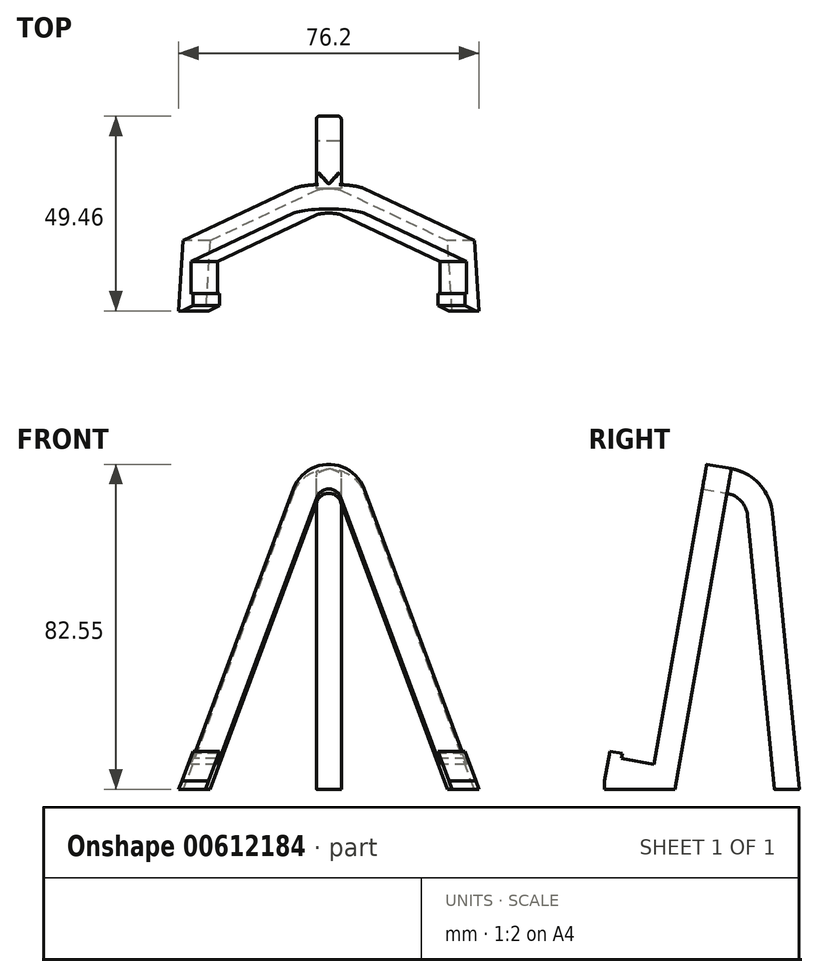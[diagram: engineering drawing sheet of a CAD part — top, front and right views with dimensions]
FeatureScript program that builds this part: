
annotation { "Feature Type Name" : "Feature", "Feature Type Description" : "" }
export const myFeature = defineFeature(function(context is Context, id is Id, definition is map)
    precondition{}
    {
        {
            var Q0;
            Q0=qCreatedBy(makeId("Right.planeOp"),FACE);
            var sketch = newSketch(context, id + "F0", { "sketchPlane" : qUnion([Q0])});
            skLineSegment(sketch, "E0", {"start": v(0, 0) * mm, "end": v(6.45, 0) * mm});
            skLineSegment(sketch, "E1", {"start": v(14.56, 82.55) * mm, "end": v(1.12, 6.35) * mm});
            skLineSegment(sketch, "E2", {"start": v(1.12, 6.35) * mm, "end": v(-7.13, 7.8) * mm});
            skLineSegment(sketch, "E3", {"start": v(-7.13, 7.8) * mm, "end": v(-6.91, 9.06) * mm});
            skLineSegment(sketch, "E4", {"start": v(-6.91, 9.06) * mm, "end": v(-10.04, 9.6) * mm});
            skLineSegment(sketch, "E5", {"start": v(-10.04, 9.6) * mm, "end": v(-11.36, 2.1) * mm});
            skLineSegment(sketch, "E6", {"start": v(14.56, 82.55) * mm, "end": v(20.8, 81.45) * mm});
            skLineSegment(sketch, "E7", {"start": v(20.8, 81.45) * mm, "end": v(12.8, 36.01) * mm});
            skLineSegment(sketch, "E8.trimOffspring", {"start": v(12.8, 36.01) * mm, "end": v(6.45, 0) * mm});
            skLineSegment(sketch, "E9", {"start": v(-11.36, 2.1) * mm, "end": v(-11.36, 0) * mm});
            skLineSegment(sketch, "E10", {"start": v(-11.36, 0) * mm, "end": v(0, 0) * mm});
            skSolve(sketch);
        }
        {
            var Q0;
            Q0=makeQuery(id+"F0.imprint","IMPRINT",FACE,{"disambiguationData":[TD([[makeQuery(id+"F0.imprint","IMPRINT",EDGE,{"derivedFrom":sQuery(id+"F0.wireOp",EDGE,"E0")}),1.0]])]});
            extrude(context, id + "F1", {"entities" : qUnion([Q0]), "endBound" : BoundingType.SYMMETRIC, "depth" : 76.2 * mm, "offsetDistance" : 25.4 * mm});
        }
        {
            var Q0;
            Q0=makeQuery(id+"F1.opExtrude","SWEPT_FACE",FACE,{"disambiguationData":[OSD([sQuery(id+"F0.wireOp",EDGE,"E1")])]});
            var sketch = newSketch(context, id + "F2", { "sketchPlane" : qUnion([Q0])});
            skLineSegment(sketch, "E11", {"start": v(-31.34, -1.97) * mm, "end": v(-2.98, 75.4) * mm});
            skLineSegment(sketch, "E12", {"start": v(2.98, 75.4) * mm, "end": v(31.34, -1.97) * mm});
            skLineSegment(sketch, "E13", {"start": v(38.1, -1.97) * mm, "end": v(31.34, -1.97) * mm});
            skLineSegment(sketch, "E14", {"start": v(38.1, -1.97) * mm, "end": v(8.94, 77.58) * mm});
            skLineSegment(sketch, "E15", {"start": v(-8.94, 77.58) * mm, "end": v(-38.1, -1.97) * mm});
            skLineSegment(sketch, "E16", {"start": v(-31.34, -1.97) * mm, "end": v(-38.1, -1.97) * mm});
            skPoint(sketch, "E17.visualSharp", {"position": v(0, 101.98) * mm});
            skArc(sketch, "E17.filletArc", {"start": v(8.94, 77.58) * mm, "mid": v(0, 83.82) * mm, "end": v(-8.94, 77.58) * mm});
            skPoint(sketch, "E18.visualSharp", {"position": v(0, 83.52) * mm});
            skArc(sketch, "E18.filletArc", {"start": v(2.98, 75.4) * mm, "mid": v(0, 77.47) * mm, "end": v(-2.98, 75.4) * mm});
            skSolve(sketch);
        }
        {
            var Q0;
            Q0 = qSketchRegion(id + "F2", true);
            extrude(context, id + "F3", {"entities" : qUnion([Q0]), "operationType" : NewBodyOperationType.INTERSECT, "endBound" : BoundingType.THROUGH_ALL, "depth" : 25.4 * mm, "offsetDistance" : 25.4 * mm, "hasSecondDirection" : true, "secondDirectionBound" : SecondDirectionBoundingType.THROUGH_ALL, "secondDirectionOppositeDirection" : true, "secondDirectionDepth" : 25.4 * mm});
        }
        {
            var Q0;
            Q0=qCreatedBy(makeId("Right.planeOp"),FACE);
            var sketch = newSketch(context, id + "F4", { "sketchPlane" : qUnion([Q0])});
            skLineSegment(sketch, "E19", {"start": v(38.1, 0) * mm, "end": v(31.72, 0) * mm});
            skLineSegment(sketch, "E20", {"start": v(19.7, 75.2) * mm, "end": v(20.8, 81.45) * mm});
            skLineSegment(sketch, "E21", {"start": v(38.1, 0) * mm, "end": v(31.24, 70.18) * mm});
            skLineSegment(sketch, "E22", {"start": v(31.72, 0) * mm, "end": v(24.92, 69.56) * mm});
            skArc(sketch, "E23", {"start": v(31.24, 70.18) * mm, "mid": v(27.92, 77.57) * mm, "end": v(20.8, 81.45) * mm});
            skArc(sketch, "E24", {"start": v(24.92, 69.56) * mm, "mid": v(23.26, 73.25) * mm, "end": v(19.7, 75.2) * mm});
            skLineSegment(sketch, "E25", {"start": v(20.8, 81.45) * mm, "end": v(14.63, 82.54) * mm, "construction": true});
            skLineSegment(sketch, "E26", {"start": v(19.7, 75.2) * mm, "end": v(13.51, 76.29) * mm, "construction": true});
            skSolve(sketch);
        }
        {
            var Q0;
            Q0=makeQuery(id+"F4.imprint","IMPRINT",FACE,{"disambiguationData":[TD([[makeQuery(id+"F4.imprint","IMPRINT",EDGE,{"derivedFrom":sQuery(id+"F4.wireOp",EDGE,"E19")}),-1.0]])]});
            extrude(context, id + "F5", {"entities" : qUnion([Q0]), "operationType" : NewBodyOperationType.ADD, "endBound" : BoundingType.SYMMETRIC, "depth" : 6.35 * mm, "offsetDistance" : 25.4 * mm});
        }
        {
            var Q0;
            Q0=makeQuery(id+"F1.opExtrude","SWEPT_FACE",FACE,{"disambiguationData":[OSD([sQuery(id+"F0.wireOp",EDGE,"E1")])]});
            var sketch = newSketch(context, id + "F6", { "sketchPlane" : qUnion([Q0])});
            skArc(sketch, "E27.0", {"start": v(8.94, 77.58) * mm, "mid": v(0, 83.82) * mm, "end": v(-8.94, 77.58) * mm});
            skLineSegment(sketch, "E28", {"start": v(-8.94, 77.58) * mm, "end": v(-8.94, 85.44) * mm});
            skLineSegment(sketch, "E29", {"start": v(-8.94, 85.44) * mm, "end": v(8.94, 85.76) * mm});
            skLineSegment(sketch, "E30", {"start": v(8.94, 85.76) * mm, "end": v(8.94, 77.58) * mm});
            skSolve(sketch);
        }
        {
            var Q0;
            Q0 = qSketchRegion(id + "F6", true);
            extrude(context, id + "F7", {"entities" : qUnion([Q0]), "operationType" : NewBodyOperationType.REMOVE, "endBound" : BoundingType.THROUGH_ALL, "oppositeDirection" : true, "depth" : 25.4 * mm, "offsetDistance" : 25.4 * mm});
        }
        {
            var Q0;
            Q0=makeQuery(id+"F3.boolean.opBoolean","INTERSECT",EDGE,{"derivedFrom":[makeQuery(id+"F1.opExtrude","SWEPT_FACE",FACE,{"disambiguationData":[OSD([sQuery(id+"F0.wireOp",EDGE,"E1")])]}),makeQuery(id+"F3.boolean.toolComplement.opBoolean","COPY",FACE,{"derivedFrom":makeQuery(id+"F3.opExtrude","SWEPT_FACE",FACE,{"disambiguationData":[OSD([sQuery(id+"F2.wireOp",EDGE,"E14")])]})})]});
            var Q1;
            Q1=makeQuery(id+"F7.boolean.opBoolean","INTERSECT",EDGE,{"derivedFrom":[makeQuery(id+"F5.opExtrude","CAP_FACE",FACE,{"disambiguationData":[OSD([sQuery(id+"F4.wireOp",EDGE,"E19"),sQuery(id+"F4.wireOp",EDGE,"E20"),sQuery(id+"F4.wireOp",EDGE,"E21"),sQuery(id+"F4.wireOp",EDGE,"E22"),sQuery(id+"F4.wireOp",EDGE,"E23"),sQuery(id+"F4.wireOp",EDGE,"E24")])],"isStart":false}),makeQuery(id+"F7.opExtrude","SWEPT_FACE",FACE,{"disambiguationData":[OSD([sQuery(id+"F6.wireOp",EDGE,"E27.0")])]})]});
            var Q2;
            Q2=makeQuery(id+"F5.opExtrude","CAP_EDGE",EDGE,{"disambiguationData":[OSD([sQuery(id+"F4.wireOp",EDGE,"E23")])],"isStart":false});
            var Q3;
            {var subQ0=makeQuery(id+"F3.boolean.toolComplement.opBoolean","COPY",FACE,{"derivedFrom":makeQuery(id+"F3.opExtrude","SWEPT_FACE",FACE,{"disambiguationData":[OSD([sQuery(id+"F2.wireOp",EDGE,"E17.filletArc")])]})});var subQ1=makeQuery(id+"F3.boolean.opBoolean","COPY",FACE,{"derivedFrom":subQ0});var subQ3=makeQuery(id+"F1.opExtrude","SWEPT_FACE",FACE,{"disambiguationData":[OSD([sQuery(id+"F0.wireOp",EDGE,"E7"),sQuery(id+"F0.wireOp",EDGE,"E8.trimOffspring")])]});Q3=makeQuery(id+"F5.boolean.opBoolean","SPLIT",EDGE,{"disambiguationData":[topologyDisambiguationEdgeConnected([subQ3,subQ1]),TD([makeQuery(id+"F3.boolean.opBoolean","COPY",FACE,{"derivedFrom":makeQuery(id+"F3.boolean.toolComplement.opBoolean","COPY",FACE,{"derivedFrom":makeQuery(id+"F3.opExtrude","SWEPT_FACE",FACE,{"disambiguationData":[OSD([sQuery(id+"F2.wireOp",EDGE,"E14")])]})})})])],"derivedFrom":makeQuery(id+"F3.boolean.opBoolean","INTERSECT",EDGE,{"derivedFrom":[subQ3,subQ0]})});}
            var Q4;
            Q4=makeQuery(id+"F3.boolean.opBoolean","INTERSECT",EDGE,{"derivedFrom":[makeQuery(id+"F1.opExtrude","SWEPT_FACE",FACE,{"disambiguationData":[OSD([sQuery(id+"F0.wireOp",EDGE,"E2")])]}),makeQuery(id+"F3.boolean.toolComplement.opBoolean","COPY",FACE,{"derivedFrom":makeQuery(id+"F3.opExtrude","SWEPT_FACE",FACE,{"disambiguationData":[OSD([sQuery(id+"F2.wireOp",EDGE,"E14")])]})})]});
            var Q5;
            Q5=makeQuery(id+"F3.boolean.opBoolean","INTERSECT",EDGE,{"derivedFrom":[makeQuery(id+"F1.opExtrude","SWEPT_FACE",FACE,{"disambiguationData":[OSD([sQuery(id+"F0.wireOp",EDGE,"E3")])]}),makeQuery(id+"F3.boolean.toolComplement.opBoolean","COPY",FACE,{"derivedFrom":makeQuery(id+"F3.opExtrude","SWEPT_FACE",FACE,{"disambiguationData":[OSD([sQuery(id+"F2.wireOp",EDGE,"E14")])]})})]});
            var Q6;
            Q6=makeQuery(id+"F3.boolean.opBoolean","INTERSECT",EDGE,{"derivedFrom":[makeQuery(id+"F1.opExtrude","SWEPT_FACE",FACE,{"disambiguationData":[OSD([sQuery(id+"F0.wireOp",EDGE,"E4")])]}),makeQuery(id+"F3.boolean.toolComplement.opBoolean","COPY",FACE,{"derivedFrom":makeQuery(id+"F3.opExtrude","SWEPT_FACE",FACE,{"disambiguationData":[OSD([sQuery(id+"F2.wireOp",EDGE,"E14")])]})})]});
            var Q7;
            Q7=makeQuery(id+"F3.boolean.opBoolean","INTERSECT",EDGE,{"derivedFrom":[makeQuery(id+"F1.opExtrude","SWEPT_FACE",FACE,{"disambiguationData":[OSD([sQuery(id+"F0.wireOp",EDGE,"E5")])]}),makeQuery(id+"F3.boolean.toolComplement.opBoolean","COPY",FACE,{"derivedFrom":makeQuery(id+"F3.opExtrude","SWEPT_FACE",FACE,{"disambiguationData":[OSD([sQuery(id+"F2.wireOp",EDGE,"E14")])]})})]});
            var Q8;
            Q8=makeQuery(id+"F3.boolean.opBoolean","MERGE",EDGE,{"derivedFrom":[makeQuery(id+"F1.opExtrude","CAP_EDGE",EDGE,{"disambiguationData":[OSD([sQuery(id+"F0.wireOp",EDGE,"PjRodM2x-iDPi-nF9E-hlY8-18HYTHsXEe14")])],"isStart":false}),makeQuery(id+"F3.boolean.toolComplement.opBoolean","COPY",EDGE,{"derivedFrom":makeQuery(id+"F3.opExtrude","SWEPT_EDGE",EDGE,{"disambiguationData":[OSD([sQuery(id+"F2.wireOp",EDGE,"E13"),sQuery(id+"F2.wireOp",EDGE,"E14")])]})})]});
            var Q9;
            {var subQ0=sQuery(id+"F0.wireOp",EDGE,"E5");var subQ1=sQuery(id+"F0.wireOp",EDGE,"PjRodM2x-iDPi-nF9E-hlY8-18HYTHsXEe14");Q9=makeQuery(id+"F3.boolean.opBoolean","SPLIT",EDGE,{"disambiguationData":[TD([makeQuery(id+"F3.boolean.toolComplement.opBoolean","COPY",FACE,{"derivedFrom":makeQuery(id+"F3.opExtrude","SWEPT_FACE",FACE,{"disambiguationData":[OSD([sQuery(id+"F2.wireOp",EDGE,"E12")])]})})])],"derivedFrom":makeQuery(id+"F1.opExtrude","SWEPT_EDGE",EDGE,{"disambiguationData":[OSD([subQ0,subQ1])]})});}
            var Q10;
            Q10=makeQuery(id+"F3.boolean.opBoolean","INTERSECT",EDGE,{"derivedFrom":[makeQuery(id+"F1.opExtrude","SWEPT_FACE",FACE,{"disambiguationData":[OSD([sQuery(id+"F0.wireOp",EDGE,"E5")])]}),makeQuery(id+"F3.boolean.toolComplement.opBoolean","COPY",FACE,{"derivedFrom":makeQuery(id+"F3.opExtrude","SWEPT_FACE",FACE,{"disambiguationData":[OSD([sQuery(id+"F2.wireOp",EDGE,"E12")])]})})]});
            var Q11;
            {var subQ0=sQuery(id+"F0.wireOp",EDGE,"E4");var subQ1=sQuery(id+"F0.wireOp",EDGE,"E5");Q11=makeQuery(id+"F3.boolean.opBoolean","SPLIT",EDGE,{"disambiguationData":[TD([makeQuery(id+"F3.boolean.toolComplement.opBoolean","COPY",FACE,{"derivedFrom":makeQuery(id+"F3.opExtrude","SWEPT_FACE",FACE,{"disambiguationData":[OSD([sQuery(id+"F2.wireOp",EDGE,"E12")])]})})])],"derivedFrom":makeQuery(id+"F1.opExtrude","SWEPT_EDGE",EDGE,{"disambiguationData":[OSD([subQ0,subQ1])]})});}
            var Q12;
            Q12=makeQuery(id+"F3.boolean.opBoolean","INTERSECT",EDGE,{"derivedFrom":[makeQuery(id+"F1.opExtrude","SWEPT_FACE",FACE,{"disambiguationData":[OSD([sQuery(id+"F0.wireOp",EDGE,"E4")])]}),makeQuery(id+"F3.boolean.toolComplement.opBoolean","COPY",FACE,{"derivedFrom":makeQuery(id+"F3.opExtrude","SWEPT_FACE",FACE,{"disambiguationData":[OSD([sQuery(id+"F2.wireOp",EDGE,"E12")])]})})]});
            var Q13;
            Q13=makeQuery(id+"F3.boolean.opBoolean","INTERSECT",EDGE,{"derivedFrom":[makeQuery(id+"F1.opExtrude","SWEPT_FACE",FACE,{"disambiguationData":[OSD([sQuery(id+"F0.wireOp",EDGE,"E2")])]}),makeQuery(id+"F3.boolean.toolComplement.opBoolean","COPY",FACE,{"derivedFrom":makeQuery(id+"F3.opExtrude","SWEPT_FACE",FACE,{"disambiguationData":[OSD([sQuery(id+"F2.wireOp",EDGE,"E12")])]})})]});
            var Q14;
            Q14=makeQuery(id+"F3.boolean.opBoolean","INTERSECT",EDGE,{"derivedFrom":[makeQuery(id+"F1.opExtrude","SWEPT_FACE",FACE,{"disambiguationData":[OSD([sQuery(id+"F0.wireOp",EDGE,"E3")])]}),makeQuery(id+"F3.boolean.toolComplement.opBoolean","COPY",FACE,{"derivedFrom":makeQuery(id+"F3.opExtrude","SWEPT_FACE",FACE,{"disambiguationData":[OSD([sQuery(id+"F2.wireOp",EDGE,"E12")])]})})]});
            var Q15;
            Q15=makeQuery(id+"F3.boolean.opBoolean","INTERSECT",EDGE,{"derivedFrom":[makeQuery(id+"F1.opExtrude","SWEPT_FACE",FACE,{"disambiguationData":[OSD([sQuery(id+"F0.wireOp",EDGE,"E1")])]}),makeQuery(id+"F3.boolean.toolComplement.opBoolean","COPY",FACE,{"derivedFrom":makeQuery(id+"F3.opExtrude","SWEPT_FACE",FACE,{"disambiguationData":[OSD([sQuery(id+"F2.wireOp",EDGE,"E12")])]})})]});
            var Q16;
            Q16=makeQuery(id+"F3.boolean.opBoolean","INTERSECT",EDGE,{"derivedFrom":[makeQuery(id+"F1.opExtrude","SWEPT_FACE",FACE,{"disambiguationData":[OSD([sQuery(id+"F0.wireOp",EDGE,"E2")])]}),makeQuery(id+"F3.boolean.toolComplement.opBoolean","COPY",FACE,{"derivedFrom":makeQuery(id+"F3.opExtrude","SWEPT_FACE",FACE,{"disambiguationData":[OSD([sQuery(id+"F2.wireOp",EDGE,"E11")])]})})]});
            var Q17;
            Q17=makeQuery(id+"F3.boolean.opBoolean","INTERSECT",EDGE,{"derivedFrom":[makeQuery(id+"F1.opExtrude","SWEPT_FACE",FACE,{"disambiguationData":[OSD([sQuery(id+"F0.wireOp",EDGE,"E3")])]}),makeQuery(id+"F3.boolean.toolComplement.opBoolean","COPY",FACE,{"derivedFrom":makeQuery(id+"F3.opExtrude","SWEPT_FACE",FACE,{"disambiguationData":[OSD([sQuery(id+"F2.wireOp",EDGE,"E11")])]})})]});
            var Q18;
            Q18=makeQuery(id+"F3.boolean.opBoolean","INTERSECT",EDGE,{"derivedFrom":[makeQuery(id+"F1.opExtrude","SWEPT_FACE",FACE,{"disambiguationData":[OSD([sQuery(id+"F0.wireOp",EDGE,"E4")])]}),makeQuery(id+"F3.boolean.toolComplement.opBoolean","COPY",FACE,{"derivedFrom":makeQuery(id+"F3.opExtrude","SWEPT_FACE",FACE,{"disambiguationData":[OSD([sQuery(id+"F2.wireOp",EDGE,"E11")])]})})]});
            var Q19;
            Q19=makeQuery(id+"F3.boolean.opBoolean","INTERSECT",EDGE,{"derivedFrom":[makeQuery(id+"F1.opExtrude","SWEPT_FACE",FACE,{"disambiguationData":[OSD([sQuery(id+"F0.wireOp",EDGE,"E5")])]}),makeQuery(id+"F3.boolean.toolComplement.opBoolean","COPY",FACE,{"derivedFrom":makeQuery(id+"F3.opExtrude","SWEPT_FACE",FACE,{"disambiguationData":[OSD([sQuery(id+"F2.wireOp",EDGE,"E11")])]})})]});
            var Q20;
            Q20=makeQuery(id+"F3.boolean.opBoolean","COPY",EDGE,{"derivedFrom":makeQuery(id+"F3.boolean.toolComplement.opBoolean","COPY",EDGE,{"derivedFrom":makeQuery(id+"F3.opExtrude","SWEPT_EDGE",EDGE,{"disambiguationData":[OSD([sQuery(id+"F2.wireOp",EDGE,"E11"),sQuery(id+"F2.wireOp",EDGE,"E16")])]})})});
            var Q21;
            {var subQ0=sQuery(id+"F0.wireOp",EDGE,"E5");var subQ1=sQuery(id+"F0.wireOp",EDGE,"PjRodM2x-iDPi-nF9E-hlY8-18HYTHsXEe14");Q21=makeQuery(id+"F3.boolean.opBoolean","SPLIT",EDGE,{"disambiguationData":[TD([makeQuery(id+"F3.boolean.toolComplement.opBoolean","COPY",FACE,{"derivedFrom":makeQuery(id+"F3.opExtrude","SWEPT_FACE",FACE,{"disambiguationData":[OSD([sQuery(id+"F2.wireOp",EDGE,"E11")])]})})])],"derivedFrom":makeQuery(id+"F1.opExtrude","SWEPT_EDGE",EDGE,{"disambiguationData":[OSD([subQ0,subQ1])]})});}
            var Q22;
            Q22=makeQuery(id+"F3.boolean.opBoolean","INTERSECT",EDGE,{"derivedFrom":[makeQuery(id+"F1.opExtrude","SWEPT_FACE",FACE,{"disambiguationData":[OSD([sQuery(id+"F0.wireOp",EDGE,"E5")])]}),makeQuery(id+"F3.boolean.toolComplement.opBoolean","COPY",FACE,{"derivedFrom":makeQuery(id+"F3.opExtrude","SWEPT_FACE",FACE,{"disambiguationData":[OSD([sQuery(id+"F2.wireOp",EDGE,"E15")])]})})]});
            var Q23;
            {var subQ0=sQuery(id+"F0.wireOp",EDGE,"E4");var subQ1=sQuery(id+"F0.wireOp",EDGE,"E5");Q23=makeQuery(id+"F3.boolean.opBoolean","SPLIT",EDGE,{"disambiguationData":[TD([makeQuery(id+"F3.boolean.toolComplement.opBoolean","COPY",FACE,{"derivedFrom":makeQuery(id+"F3.opExtrude","SWEPT_FACE",FACE,{"disambiguationData":[OSD([sQuery(id+"F2.wireOp",EDGE,"E11")])]})})])],"derivedFrom":makeQuery(id+"F1.opExtrude","SWEPT_EDGE",EDGE,{"disambiguationData":[OSD([subQ0,subQ1])]})});}
            var Q24;
            Q24=makeQuery(id+"F3.boolean.opBoolean","INTERSECT",EDGE,{"derivedFrom":[makeQuery(id+"F1.opExtrude","SWEPT_FACE",FACE,{"disambiguationData":[OSD([sQuery(id+"F0.wireOp",EDGE,"E4")])]}),makeQuery(id+"F3.boolean.toolComplement.opBoolean","COPY",FACE,{"derivedFrom":makeQuery(id+"F3.opExtrude","SWEPT_FACE",FACE,{"disambiguationData":[OSD([sQuery(id+"F2.wireOp",EDGE,"E15")])]})})]});
            var Q25;
            Q25=makeQuery(id+"F3.boolean.opBoolean","INTERSECT",EDGE,{"derivedFrom":[makeQuery(id+"F1.opExtrude","SWEPT_FACE",FACE,{"disambiguationData":[OSD([sQuery(id+"F0.wireOp",EDGE,"E3")])]}),makeQuery(id+"F3.boolean.toolComplement.opBoolean","COPY",FACE,{"derivedFrom":makeQuery(id+"F3.opExtrude","SWEPT_FACE",FACE,{"disambiguationData":[OSD([sQuery(id+"F2.wireOp",EDGE,"E15")])]})})]});
            var Q26;
            Q26=makeQuery(id+"F3.boolean.opBoolean","INTERSECT",EDGE,{"derivedFrom":[makeQuery(id+"F1.opExtrude","SWEPT_FACE",FACE,{"disambiguationData":[OSD([sQuery(id+"F0.wireOp",EDGE,"E2")])]}),makeQuery(id+"F3.boolean.toolComplement.opBoolean","COPY",FACE,{"derivedFrom":makeQuery(id+"F3.opExtrude","SWEPT_FACE",FACE,{"disambiguationData":[OSD([sQuery(id+"F2.wireOp",EDGE,"E15")])]})})]});
            var Q27;
            Q27=makeQuery(id+"F3.boolean.opBoolean","INTERSECT",EDGE,{"derivedFrom":[makeQuery(id+"F1.opExtrude","SWEPT_FACE",FACE,{"disambiguationData":[OSD([sQuery(id+"F0.wireOp",EDGE,"E7"),sQuery(id+"F0.wireOp",EDGE,"E8.trimOffspring")])]}),makeQuery(id+"F3.boolean.toolComplement.opBoolean","COPY",FACE,{"derivedFrom":makeQuery(id+"F3.opExtrude","SWEPT_FACE",FACE,{"disambiguationData":[OSD([sQuery(id+"F2.wireOp",EDGE,"E15")])]})})]});
            var Q28;
            Q28=makeQuery(id+"F7.boolean.opBoolean","INTERSECT",EDGE,{"derivedFrom":[makeQuery(id+"F5.opExtrude","CAP_FACE",FACE,{"disambiguationData":[OSD([sQuery(id+"F4.wireOp",EDGE,"E19"),sQuery(id+"F4.wireOp",EDGE,"E20"),sQuery(id+"F4.wireOp",EDGE,"E21"),sQuery(id+"F4.wireOp",EDGE,"E22"),sQuery(id+"F4.wireOp",EDGE,"E23"),sQuery(id+"F4.wireOp",EDGE,"E24")])],"isStart":true}),makeQuery(id+"F7.opExtrude","SWEPT_FACE",FACE,{"disambiguationData":[OSD([sQuery(id+"F6.wireOp",EDGE,"E27.0")])]})]});
            var Q29;
            Q29=makeQuery(id+"F5.opExtrude","CAP_EDGE",EDGE,{"disambiguationData":[OSD([sQuery(id+"F4.wireOp",EDGE,"E23")])],"isStart":true});
            var Q30;
            Q30=makeQuery(id+"F7.boolean.opBoolean","INTERSECT",EDGE,{"disambiguationData":[OD(0.0)],"derivedFrom":[makeQuery(id+"F5.opExtrude","SWEPT_FACE",FACE,{"disambiguationData":[OSD([sQuery(id+"F4.wireOp",EDGE,"E23")])]}),makeQuery(id+"F7.opExtrude","SWEPT_FACE",FACE,{"disambiguationData":[OSD([sQuery(id+"F6.wireOp",EDGE,"E27.0")])]})]});
            var Q31;
            Q31=makeQuery(id+"F7.boolean.opBoolean","INTERSECT",EDGE,{"disambiguationData":[OD(1.0)],"derivedFrom":[makeQuery(id+"F5.opExtrude","SWEPT_FACE",FACE,{"disambiguationData":[OSD([sQuery(id+"F4.wireOp",EDGE,"E23")])]}),makeQuery(id+"F7.opExtrude","SWEPT_FACE",FACE,{"disambiguationData":[OSD([sQuery(id+"F6.wireOp",EDGE,"E27.0")])]})]});
            var Q32;
            Q32=makeQuery(id+"F5.opExtrude","CAP_EDGE",EDGE,{"disambiguationData":[OSD([sQuery(id+"F4.wireOp",EDGE,"E24")])],"isStart":true});
            var Q33;
            Q33=makeQuery(id+"F5.opExtrude","CAP_EDGE",EDGE,{"disambiguationData":[OSD([sQuery(id+"F4.wireOp",EDGE,"E24")])],"isStart":false});
            var Q34;
            Q34=makeQuery(id+"F3.boolean.opBoolean","COPY",EDGE,{"derivedFrom":makeQuery(id+"F3.boolean.toolComplement.opBoolean","COPY",EDGE,{"derivedFrom":makeQuery(id+"F3.opExtrude","SWEPT_EDGE",EDGE,{"disambiguationData":[OSD([sQuery(id+"F2.wireOp",EDGE,"E12"),sQuery(id+"F2.wireOp",EDGE,"E13")])]})})});
            var Q35;
            Q35=makeQuery(id+"F3.boolean.opBoolean","INTERSECT",EDGE,{"derivedFrom":[makeQuery(id+"F1.opExtrude","SWEPT_FACE",FACE,{"disambiguationData":[OSD([sQuery(id+"F0.wireOp",EDGE,"E7"),sQuery(id+"F0.wireOp",EDGE,"E8.trimOffspring")])]}),makeQuery(id+"F3.boolean.toolComplement.opBoolean","COPY",FACE,{"derivedFrom":makeQuery(id+"F3.opExtrude","SWEPT_FACE",FACE,{"disambiguationData":[OSD([sQuery(id+"F2.wireOp",EDGE,"E12")])]})})]});
            var Q36;
            Q36=makeQuery(id+"F3.boolean.opBoolean","MERGE",EDGE,{"derivedFrom":[makeQuery(id+"F1.opExtrude","CAP_EDGE",EDGE,{"disambiguationData":[OSD([sQuery(id+"F0.wireOp",EDGE,"PjRodM2x-iDPi-nF9E-hlY8-18HYTHsXEe14")])],"isStart":true}),makeQuery(id+"F3.boolean.toolComplement.opBoolean","COPY",EDGE,{"derivedFrom":makeQuery(id+"F3.opExtrude","SWEPT_EDGE",EDGE,{"disambiguationData":[OSD([sQuery(id+"F2.wireOp",EDGE,"E15"),sQuery(id+"F2.wireOp",EDGE,"E16")])]})})]});
            fillet(context, id + "F8", {"entities" : qUnion([Q0, Q1, Q2, Q3, Q4, Q5, Q6, Q7, Q8, Q9, Q10, Q11, Q12, Q13, Q14, Q15, Q16, Q17, Q18, Q19, Q20, Q21, Q22, Q23, Q24, Q25, Q26, Q27, Q28, Q29, Q30, Q31, Q32, Q33, Q34, Q35, Q36]), "radius" : 0.8 * mm, "tangentPropagation" : true, "allowEdgeOverflow" : false});
        }
    });
